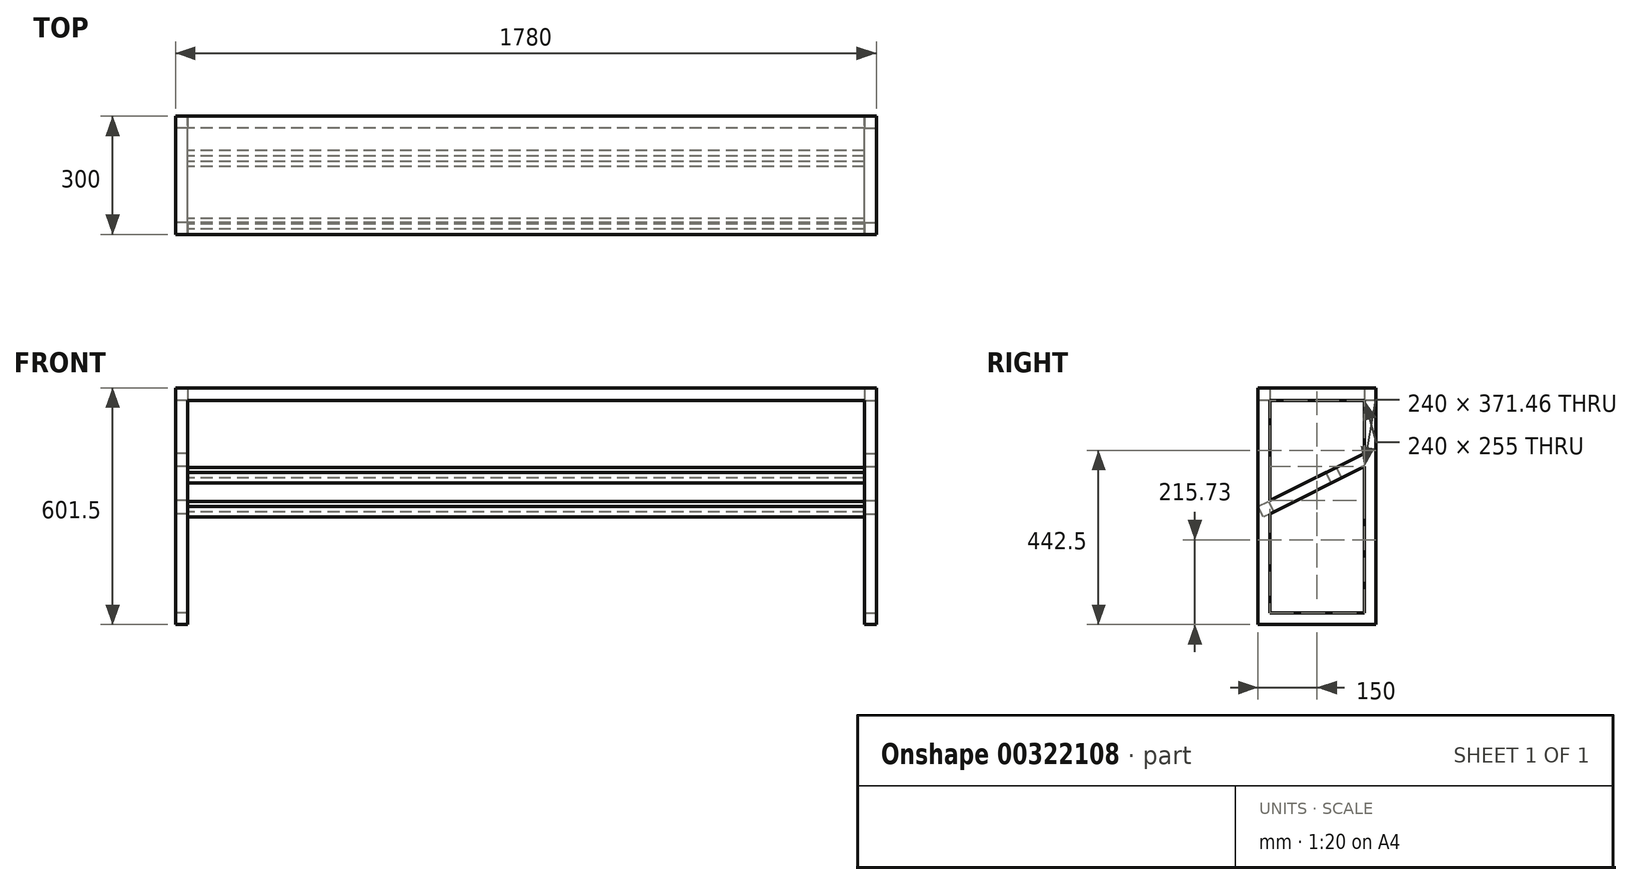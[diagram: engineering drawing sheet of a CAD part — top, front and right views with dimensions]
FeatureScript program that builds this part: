
annotation { "Feature Type Name" : "Feature", "Feature Type Description" : "" }
export const myFeature = defineFeature(function(context is Context, id is Id, definition is map)
    precondition{}
    {
        {
            var Q0;
            Q0=qCreatedBy(makeId("Right.planeOp"),FACE);
            cPlane(context, id + "F0", {"entities" : qUnion([Q0]), "cplaneType" : CPlaneType.OFFSET, "offset" : 1780 * mm, "width" : 150 * mm, "height" : 150 * mm});
        }
        {
            var Q0;
            Q0=qCreatedBy(makeId("Right.planeOp"),FACE);
            cPlane(context, id + "F1", {"entities" : qUnion([Q0]), "cplaneType" : CPlaneType.OFFSET, "offset" : (1780 / 2) * mm, "width" : 150 * mm, "height" : 150 * mm});
        }
        {
            var Q0;
            Q0=qCreatedBy(makeId("Right.planeOp"),FACE);
            var sketch = newSketch(context, id + "F2", { "sketchPlane" : qUnion([Q0])});
            skLineSegment(sketch, "E0", {"start": v(0, 0) * mm, "end": v(0, 600) * mm});
            skPoint(sketch, "E1.orphan", {"position": v(0, 450) * mm});
            skLineSegment(sketch, "E2.MirrorCS", {"start": v(-270, 281.46) * mm, "end": v(-270, 30) * mm});
            skLineSegment(sketch, "E3.MirrorCS", {"start": v(-30, 435) * mm, "end": v(-30, 570) * mm});
            skLineSegment(sketch, "E4.MirrorCS", {"start": v(-270, 281.46) * mm, "end": v(-30, 401.46) * mm});
            skLineSegment(sketch, "E5.MirrorCS", {"start": v(-270, 315) * mm, "end": v(-30, 435) * mm});
            skLineSegment(sketch, "E6.MirrorCS", {"start": v(-270, 570) * mm, "end": v(-270, 315) * mm});
            skLineSegment(sketch, "E7.MirrorCS", {"start": v(-270, 30) * mm, "end": v(-30, 30) * mm});
            skLineSegment(sketch, "E8.MirrorCS", {"start": v(-30, 30) * mm, "end": v(-30, 401.46) * mm});
            skLineSegment(sketch, "E9.MirrorCS", {"start": v(-30, 570) * mm, "end": v(-270, 570) * mm});
            skLineSegment(sketch, "E10.MirrorCS", {"start": v(-300, 0) * mm, "end": v(0, 0) * mm});
            skLineSegment(sketch, "E11.MirrorCS", {"start": v(-300, 600) * mm, "end": v(-300, 0) * mm});
            skLineSegment(sketch, "E12.MirrorCS", {"start": v(0, 600) * mm, "end": v(-300, 600) * mm});
            skSolve(sketch);
        }
        {
            var Q0;
            Q0 = qSketchRegion(id + "F2", true);
            extrude(context, id + "F3", {"entities" : qUnion([Q0]), "depth" : 30 * mm});
        }
        {
            var Q0;
            Q0=qCreatedBy(id+"F0.planeOp",FACE);
            var sketch = newSketch(context, id + "F4", { "sketchPlane" : qUnion([Q0])});
            skLineSegment(sketch, "E13", {"start": v(0, 0) * mm, "end": v(0, 600) * mm});
            skPoint(sketch, "E14.orphan", {"position": v(0, 450) * mm});
            skLineSegment(sketch, "E15.MirrorCS", {"start": v(-270, 281.46) * mm, "end": v(-270, 30) * mm});
            skLineSegment(sketch, "E16.MirrorCS", {"start": v(-30, 435) * mm, "end": v(-30, 570) * mm});
            skLineSegment(sketch, "E17.MirrorCS", {"start": v(-270, 281.46) * mm, "end": v(-30, 401.46) * mm});
            skLineSegment(sketch, "E18.MirrorCS", {"start": v(-270, 315) * mm, "end": v(-30, 435) * mm});
            skLineSegment(sketch, "E19.MirrorCS", {"start": v(-270, 570) * mm, "end": v(-270, 315) * mm});
            skLineSegment(sketch, "E20.MirrorCS", {"start": v(-270, 30) * mm, "end": v(-30, 30) * mm});
            skLineSegment(sketch, "E21.MirrorCS", {"start": v(-30, 30) * mm, "end": v(-30, 401.46) * mm});
            skLineSegment(sketch, "E22.MirrorCS", {"start": v(-30, 570) * mm, "end": v(-270, 570) * mm});
            skLineSegment(sketch, "E23.MirrorCS", {"start": v(-300, 0) * mm, "end": v(0, 0) * mm});
            skLineSegment(sketch, "E24.MirrorCS", {"start": v(-300, 600) * mm, "end": v(-300, 0) * mm});
            skLineSegment(sketch, "E25.MirrorCS", {"start": v(0, 600) * mm, "end": v(-300, 600) * mm});
            skSolve(sketch);
        }
        {
            var Q0;
            Q0 = qSketchRegion(id + "F4", true);
            extrude(context, id + "F5", {"entities" : qUnion([Q0]), "oppositeDirection" : true, "depth" : 30 * mm});
        }
        {
            var Q0;
            Q0=qCreatedBy(id+"F1.planeOp",FACE);
            var sketch = newSketch(context, id + "F6", { "sketchPlane" : qUnion([Q0])});
            skLineSegment(sketch, "E26", {"start": v(-300, 300) * mm, "end": v(-273.17, 313.42) * mm});
            skLineSegment(sketch, "E27", {"start": v(-286.58, 273.17) * mm, "end": v(-300, 300) * mm});
            skLineSegment(sketch, "E28", {"start": v(-273.17, 313.42) * mm, "end": v(-259.75, 286.58) * mm});
            skLineSegment(sketch, "E29.trimOffspring", {"start": v(-259.75, 286.58) * mm, "end": v(-286.58, 273.17) * mm});
            skLineSegment(sketch, "E30.bottom", {"start": v(0, 600) * mm, "end": v(-30, 600) * mm});
            skLineSegment(sketch, "E30.top", {"start": v(0, 570) * mm, "end": v(-30, 570) * mm});
            skLineSegment(sketch, "E30.left", {"start": v(0, 600) * mm, "end": v(0, 570) * mm});
            skLineSegment(sketch, "E30.right", {"start": v(-30, 600) * mm, "end": v(-30, 570) * mm});
            skLineSegment(sketch, "E31.bottom", {"start": v(-270, 600) * mm, "end": v(-300, 600) * mm});
            skLineSegment(sketch, "E31.top", {"start": v(-270, 570) * mm, "end": v(-300, 570) * mm});
            skLineSegment(sketch, "E31.left", {"start": v(-270, 600) * mm, "end": v(-270, 570) * mm});
            skLineSegment(sketch, "E31.right", {"start": v(-300, 600) * mm, "end": v(-300, 570) * mm});
            skLineSegment(sketch, "E32", {"start": v(-127.82, 386.09) * mm, "end": v(-100.99, 399.5) * mm});
            skLineSegment(sketch, "E33", {"start": v(-114.4, 359.26) * mm, "end": v(-87.57, 372.67) * mm});
            skLineSegment(sketch, "E34", {"start": v(-127.82, 386.09) * mm, "end": v(-114.4, 359.26) * mm});
            skLineSegment(sketch, "E35", {"start": v(-100.99, 399.5) * mm, "end": v(-87.57, 372.67) * mm});
            skSolve(sketch);
        }
        {
            var Q0;
            Q0 = qSketchRegion(id + "F6", true);
            extrude(context, id + "F7", {"entities" : qUnion([Q0]), "operationType" : NewBodyOperationType.ADD, "endBound" : BoundingType.UP_TO_NEXT, "depth" : 25 * mm, "hasSecondDirection" : true, "secondDirectionBound" : SecondDirectionBoundingType.UP_TO_NEXT, "secondDirectionOppositeDirection" : true, "secondDirectionDepth" : 25 * mm});
        }
        {
            var Q0;
            Q0=makeQuery(id+"F7.boolean.opBoolean","MERGE",FACE,{"derivedFrom":[makeQuery(id+"F3.opExtrude","SWEPT_FACE",FACE,{"disambiguationData":[OSD([sQuery(id+"F2.wireOp",EDGE,"E12.MirrorCS")])]}),makeQuery(id+"F5.opExtrude","SWEPT_FACE",FACE,{"disambiguationData":[OSD([sQuery(id+"F4.wireOp",EDGE,"E25.MirrorCS")])]}),makeQuery(id+"F7.opExtrude","SWEPT_FACE",FACE,{"disambiguationData":[OSD([sQuery(id+"F6.wireOp",EDGE,"E30.bottom")])]}),makeQuery(id+"F7.opExtrude","SWEPT_FACE",FACE,{"disambiguationData":[OSD([sQuery(id+"F6.wireOp",EDGE,"E31.bottom")])]})]});
            var sketch = newSketch(context, id + "F8", { "sketchPlane" : qUnion([Q0])});
            skLineSegment(sketch, "E36.bottom", {"start": v(0, 0) * mm, "end": v(1780, 0) * mm});
            skLineSegment(sketch, "E36.top", {"start": v(0, -300) * mm, "end": v(1780, -300) * mm});
            skLineSegment(sketch, "E36.left", {"start": v(0, 0) * mm, "end": v(0, -300) * mm});
            skLineSegment(sketch, "E36.right", {"start": v(1780, 0) * mm, "end": v(1780, -300) * mm});
            skSolve(sketch);
        }
        {
            var Q0;
            Q0 = qSketchRegion(id + "F8", true);
            extrude(context, id + "F9", {"entities" : qUnion([Q0]), "operationType" : NewBodyOperationType.ADD, "depth" : 1.5 * mm});
        }
    });
